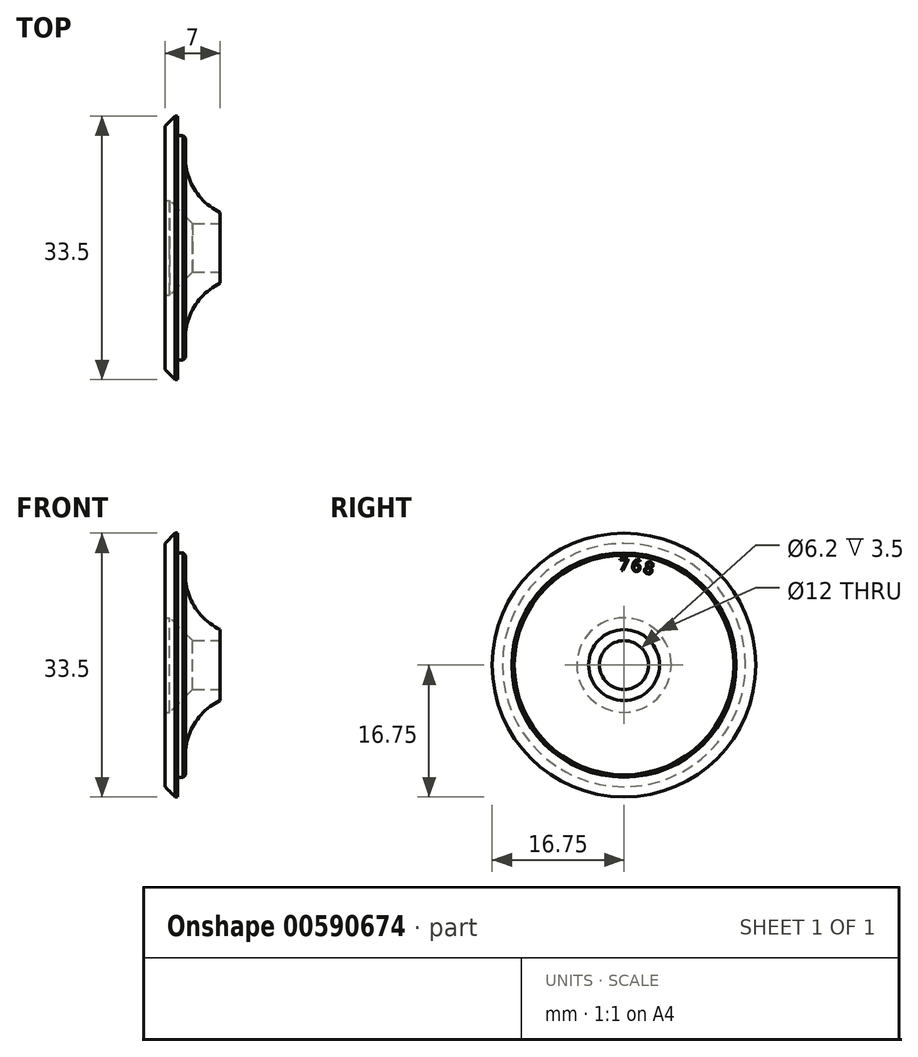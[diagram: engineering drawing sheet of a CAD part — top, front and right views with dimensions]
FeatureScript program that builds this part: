
annotation { "Feature Type Name" : "Feature", "Feature Type Description" : "" }
export const myFeature = defineFeature(function(context is Context, id is Id, definition is map)
    precondition{}
    {
        {
            var Q0;
            Q0=qCreatedBy(makeId("Top.planeOp"),FACE);
            var sketch = newSketch(context, id + "F0", { "sketchPlane" : qUnion([Q0])});
            skLineSegment(sketch, "E0", {"start": v(-4.4, 14.25) * mm, "end": v(-5.4, 14.25) * mm});
            skLineSegment(sketch, "E1", {"start": v(-5.4, 14.25) * mm, "end": v(-5.4, 16.75) * mm});
            skLineSegment(sketch, "E2", {"start": v(0, 0) * mm, "end": v(-7, 0) * mm, "construction": true});
            skLineSegment(sketch, "E3", {"start": v(-3.5, 3.1) * mm, "end": v(0, 3.1) * mm});
            skLineSegment(sketch, "E4", {"start": v(0, 3.1) * mm, "end": v(0, 4.5) * mm});
            skLineSegment(sketch, "E5", {"start": v(-5.4, 16.75) * mm, "end": v(-7, 16.75) * mm});
            skLineSegment(sketch, "E6", {"start": v(-7, 6) * mm, "end": v(-7, 16.75) * mm});
            skLineSegment(sketch, "E7", {"start": v(-6.4, 6) * mm, "end": v(-3.5, 3.1) * mm});
            skLineSegment(sketch, "E8", {"start": v(-7, 6) * mm, "end": v(-6.4, 6) * mm});
            skLineSegment(sketch, "E9", {"start": v(-4.4, 14.25) * mm, "end": v(-4.4, 11.5) * mm});
            skArc(sketch, "E10", {"start": v(-4.4, 11.5) * mm, "mid": v(-3.2, 7.37) * mm, "end": v(0, 4.5) * mm});
            skLineSegment(sketch, "E11", {"start": v(-5.7, 16.75) * mm, "end": v(-7, 15.45) * mm});
            skSolve(sketch);
        }
        {
            var Q0;
            Q0=makeQuery(id+"F0.imprint","IMPRINT",FACE,{"disambiguationData":[TD([[makeQuery(id+"F0.imprint","IMPRINT",EDGE,{"derivedFrom":sQuery(id+"F0.wireOp",EDGE,"E0")}),1.0]])]});
            var Q1;
            Q1=sQuery(id+"F0.wireOp",EDGE,"E2");
            revolve(context, id + "F1", {"entities" : qUnion([Q0]), "axis" : qUnion([Q1]), "revolveType" : RevolveType.FULL});
        }
        {
            var Q0;
            Q0=makeQuery(id+"F1.opRevolve","SWEPT_FACE",FACE,{"disambiguationData":[OSD([sQuery(id+"F0.wireOp",EDGE,"E6")])]});
            var sketch = newSketch(context, id + "F2", { "sketchPlane" : qUnion([Q0])});
            skCircle(sketch, "E12", {"center": v(0, 0) * mm, "radius": 16.75 * mm});
            skLineSegment(sketch, "E13", {"start": v(-3, 11.75) * mm, "end": v(-3, -16.48) * mm});
            skLineSegment(sketch, "E14.MirrorCS", {"start": v(3, 11.75) * mm, "end": v(3, -16.48) * mm});
            skLineSegment(sketch, "E15", {"start": v(-9, -14.13) * mm, "end": v(-9, 1.29) * mm});
            skLineSegment(sketch, "E16", {"start": v(-9, 1.29) * mm, "end": v(-3, -7.28) * mm});
            skLineSegment(sketch, "E17", {"start": v(3, -7.28) * mm, "end": v(9, 1.29) * mm});
            skLineSegment(sketch, "E18", {"start": v(9, 1.29) * mm, "end": v(9, -14.13) * mm});
            skLineSegment(sketch, "E19", {"start": v(-15, -7.45) * mm, "end": v(-15, 7.45) * mm});
            skLineSegment(sketch, "E20", {"start": v(-9, 11.75) * mm, "end": v(-3, 3.18) * mm});
            skLineSegment(sketch, "E21", {"start": v(3, 3.18) * mm, "end": v(9, 11.75) * mm});
            skLineSegment(sketch, "E22", {"start": v(15, 7.45) * mm, "end": v(15, -7.45) * mm});
            skLineSegment(sketch, "E23", {"start": v(0, 16.75) * mm, "end": v(0, -16.75) * mm, "construction": true});
            skLineSegment(sketch, "E24", {"start": v(3, 11.75) * mm, "end": v(-3, 11.75) * mm});
            skLineSegment(sketch, "E25", {"start": v(9, 1.29) * mm, "end": v(15, 1.29) * mm, "construction": true});
            skLineSegment(sketch, "E26", {"start": v(-9, 1.29) * mm, "end": v(-15, 1.29) * mm, "construction": true});
            skLineSegment(sketch, "E27", {"start": v(-3, 3.18) * mm, "end": v(-7.91, -0.26) * mm, "construction": true});
            skLineSegment(sketch, "E28", {"start": v(3, -7.28) * mm, "end": v(9, -7.28) * mm, "construction": true});
            skLineSegment(sketch, "E29", {"start": v(-9, 11.75) * mm, "end": v(-11.94, 11.75) * mm});
            skLineSegment(sketch, "E30", {"start": v(9, 11.75) * mm, "end": v(11.94, 11.75) * mm});
            skArc(sketch, "E31", {"start": v(-5, 6.04) * mm, "mid": v(-3.77, 5.62) * mm, "end": v(-3, 6.67) * mm});
            skArc(sketch, "E32", {"start": v(3, 6.67) * mm, "mid": v(3.77, 5.62) * mm, "end": v(5, 6.04) * mm});
            skSolve(sketch);
        }
        {
            var Q0;
            Q0=makeQuery(id+"F1.opRevolve","SWEPT_FACE",FACE,{"disambiguationData":[OSD([sQuery(id+"F0.wireOp",EDGE,"E9")])]});
            var sketch = newSketch(context, id + "F3", { "sketchPlane" : qUnion([Q0])});
            skCircle(sketch, "E33", {"center": v(0, 0) * mm, "radius": 12 * mm, "construction": true});
            skCircle(sketch, "E34.cCircle", {"center": v(0, 0) * mm, "radius": 11.98 * mm, "construction": true});
            skLineSegment(sketch, "E34.0", {"start": v(-2.98, -11.62) * mm, "end": v(-4.42, -11.16) * mm});
            skLineSegment(sketch, "E34.1", {"start": v(-4.42, -11.16) * mm, "end": v(-5.78, -10.52) * mm});
            skLineSegment(sketch, "E34.2", {"start": v(-5.78, -10.52) * mm, "end": v(-7.05, -9.7) * mm});
            skLineSegment(sketch, "E34.3", {"start": v(-7.05, -9.7) * mm, "end": v(-8.21, -8.75) * mm});
            skLineSegment(sketch, "E34.4", {"start": v(-8.21, -8.75) * mm, "end": v(-9.25, -7.65) * mm});
            skLineSegment(sketch, "E34.5", {"start": v(-9.25, -7.65) * mm, "end": v(-10.13, -6.43) * mm});
            skLineSegment(sketch, "E34.6", {"start": v(-10.13, -6.43) * mm, "end": v(-10.86, -5.1) * mm});
            skLineSegment(sketch, "E34.7", {"start": v(-10.86, -5.1) * mm, "end": v(-11.41, -3.7) * mm});
            skLineSegment(sketch, "E34.8", {"start": v(-11.41, -3.7) * mm, "end": v(-11.79, -2.25) * mm});
            skLineSegment(sketch, "E34.9", {"start": v(-11.79, -2.25) * mm, "end": v(-11.98, -0.75) * mm});
            skLineSegment(sketch, "E34.10", {"start": v(-11.98, -0.75) * mm, "end": v(-11.98, 0.75) * mm});
            skLineSegment(sketch, "E34.11", {"start": v(-11.98, 0.75) * mm, "end": v(-11.79, 2.25) * mm});
            skLineSegment(sketch, "E34.12", {"start": v(-11.79, 2.25) * mm, "end": v(-11.41, 3.7) * mm});
            skLineSegment(sketch, "E34.13", {"start": v(-11.41, 3.7) * mm, "end": v(-10.86, 5.1) * mm});
            skLineSegment(sketch, "E34.14", {"start": v(-10.86, 5.1) * mm, "end": v(-10.13, 6.43) * mm});
            skLineSegment(sketch, "E34.15", {"start": v(-10.13, 6.43) * mm, "end": v(-9.25, 7.65) * mm});
            skLineSegment(sketch, "E34.16", {"start": v(-9.25, 7.65) * mm, "end": v(-8.21, 8.75) * mm});
            skLineSegment(sketch, "E34.17", {"start": v(-8.21, 8.75) * mm, "end": v(-7.05, 9.7) * mm});
            skLineSegment(sketch, "E34.18", {"start": v(-7.05, 9.7) * mm, "end": v(-5.78, 10.52) * mm});
            skLineSegment(sketch, "E34.19", {"start": v(-5.78, 10.52) * mm, "end": v(-4.42, 11.16) * mm});
            skLineSegment(sketch, "E34.20", {"start": v(-4.42, 11.16) * mm, "end": v(-2.98, 11.62) * mm});
            skLineSegment(sketch, "E34.21", {"start": v(-2.98, 11.62) * mm, "end": v(-1.5, 11.9) * mm});
            skLineSegment(sketch, "E34.22", {"start": v(-1.5, 11.9) * mm, "end": v(0, 12) * mm});
            skLineSegment(sketch, "E34.23", {"start": v(0, 12) * mm, "end": v(1.5, 11.9) * mm});
            skLineSegment(sketch, "E34.24", {"start": v(1.5, 11.9) * mm, "end": v(2.98, 11.62) * mm});
            skLineSegment(sketch, "E34.25", {"start": v(2.98, 11.62) * mm, "end": v(4.42, 11.16) * mm});
            skLineSegment(sketch, "E34.26", {"start": v(4.42, 11.16) * mm, "end": v(5.78, 10.52) * mm});
            skLineSegment(sketch, "E34.27", {"start": v(5.78, 10.52) * mm, "end": v(7.05, 9.7) * mm});
            skLineSegment(sketch, "E34.28", {"start": v(7.05, 9.7) * mm, "end": v(8.21, 8.75) * mm});
            skLineSegment(sketch, "E34.29", {"start": v(8.21, 8.75) * mm, "end": v(9.25, 7.65) * mm});
            skLineSegment(sketch, "E34.30", {"start": v(9.25, 7.65) * mm, "end": v(10.13, 6.43) * mm});
            skLineSegment(sketch, "E34.31", {"start": v(10.13, 6.43) * mm, "end": v(10.86, 5.1) * mm});
            skLineSegment(sketch, "E34.32", {"start": v(10.86, 5.1) * mm, "end": v(11.41, 3.7) * mm});
            skLineSegment(sketch, "E34.33", {"start": v(11.41, 3.7) * mm, "end": v(11.79, 2.25) * mm});
            skLineSegment(sketch, "E34.34", {"start": v(11.79, 2.25) * mm, "end": v(11.98, 0.75) * mm});
            skLineSegment(sketch, "E34.35", {"start": v(11.98, 0.75) * mm, "end": v(11.98, -0.75) * mm});
            skLineSegment(sketch, "E34.36", {"start": v(11.98, -0.75) * mm, "end": v(11.79, -2.25) * mm});
            skLineSegment(sketch, "E34.37", {"start": v(11.79, -2.25) * mm, "end": v(11.41, -3.7) * mm});
            skLineSegment(sketch, "E34.38", {"start": v(11.41, -3.7) * mm, "end": v(10.86, -5.1) * mm});
            skLineSegment(sketch, "E34.39", {"start": v(10.86, -5.1) * mm, "end": v(10.13, -6.43) * mm});
            skLineSegment(sketch, "E34.40", {"start": v(10.13, -6.43) * mm, "end": v(9.25, -7.65) * mm});
            skLineSegment(sketch, "E34.41", {"start": v(9.25, -7.65) * mm, "end": v(8.21, -8.75) * mm});
            skLineSegment(sketch, "E34.42", {"start": v(8.21, -8.75) * mm, "end": v(7.05, -9.7) * mm});
            skLineSegment(sketch, "E34.43", {"start": v(7.05, -9.7) * mm, "end": v(5.78, -10.52) * mm});
            skLineSegment(sketch, "E34.44", {"start": v(5.78, -10.52) * mm, "end": v(4.42, -11.16) * mm});
            skLineSegment(sketch, "E34.45", {"start": v(4.42, -11.16) * mm, "end": v(2.98, -11.62) * mm});
            skLineSegment(sketch, "E34.46", {"start": v(2.98, -11.62) * mm, "end": v(1.5, -11.9) * mm});
            skLineSegment(sketch, "E34.47", {"start": v(1.5, -11.9) * mm, "end": v(0, -12) * mm});
            skLineSegment(sketch, "E34.48", {"start": v(0, -12) * mm, "end": v(-1.5, -11.9) * mm});
            skLineSegment(sketch, "E34.49", {"start": v(-1.5, -11.9) * mm, "end": v(-2.98, -11.62) * mm});
            skPoint(sketch, "E34.0.midPoint", {"position": v(-3.7, -11.4) * mm});
            skLineSegment(sketch, "E35", {"start": v(0, 0) * mm, "end": v(0, 12) * mm, "construction": true});
            skLineSegment(sketch, "E36", {"start": v(0, 0) * mm, "end": v(1.5, 11.9) * mm, "construction": true});
            skLineSegment(sketch, "E37", {"start": v(0, 0) * mm, "end": v(2.98, 11.62) * mm, "construction": true});
            skText(sketch, "E38", { "text": "7", "fontName": "OpenSans-Regular.ttf"});
            skText(sketch, "E39", { "text": "8", "fontName": "OpenSans-Regular.ttf"});
            skText(sketch, "E40", { "text": "6", "fontName": "OpenSans-Regular.ttf"});
            skText(sketch, "E41", { "text": "-", "fontName": "OpenSans-Regular.ttf"});
            skLineSegment(sketch, "E42", {"start": v(0, 0) * mm, "end": v(5.78, 10.52) * mm, "construction": true});
            skLineSegment(sketch, "E43", {"start": v(8.21, 8.75) * mm, "end": v(0, 0) * mm, "construction": true});
            const initialGuessF3  = {"E38": [-0.00061, 0.012, 1, 0, 0.0015], "E39": [0.0024, 0.01177, 0.96858, -0.24869, 0.0015], "E40": [0.0009, 0.01198, 0.99211, -0.12533, 0.0015], "E41": [0.00547, 0.01069, 0.8763, -0.48175, 0.0015]};
            skSetInitialGuess(sketch, initialGuessF3);
            skSolve(sketch);
        }
        {
            var Q0;
            Q0=makeQuery(id+"F3.imprint","IMPRINT",FACE,{"disambiguationData":[TD([[makeQuery(id+"F3.imprint","IMPRINT",EDGE,{"derivedFrom":sQuery(id+"F3.wireOp",EDGE,"E38.sketch_text.stroke-0")}),-1.0]])]});
            var Q1;
            Q1=makeQuery(id+"F3.imprint","IMPRINT",FACE,{"disambiguationData":[TD([[makeQuery(id+"F3.imprint","IMPRINT",EDGE,{"derivedFrom":sQuery(id+"F3.wireOp",EDGE,"E40.sketch_text.stroke-0")}),-1.0]])]});
            var Q2;
            Q2=makeQuery(id+"F3.imprint","IMPRINT",FACE,{"disambiguationData":[TD([[makeQuery(id+"F3.imprint","IMPRINT",EDGE,{"derivedFrom":sQuery(id+"F3.wireOp",EDGE,"E39.sketch_text.stroke-0")}),-1.0]])]});
            extrude(context, id + "F4", {"entities" : qUnion([Q0, Q1, Q2]), "operationType" : NewBodyOperationType.REMOVE, "oppositeDirection" : true, "depth" : 0.05 * mm, "offsetDistance" : 25 * mm});
        }
        {
            var Q0;
            Q0=makeQuery(id+"F1.opRevolve","SWEPT_EDGE",EDGE,{"disambiguationData":[OSD([sQuery(id+"F0.wireOp",EDGE,"E0"),sQuery(id+"F0.wireOp",EDGE,"E9")])]});
            chamfer(context, id + "F5", {"entities" : qUnion([Q0]), "width" : 0.3 * mm, "tangentPropagation" : true});
        }
    });
